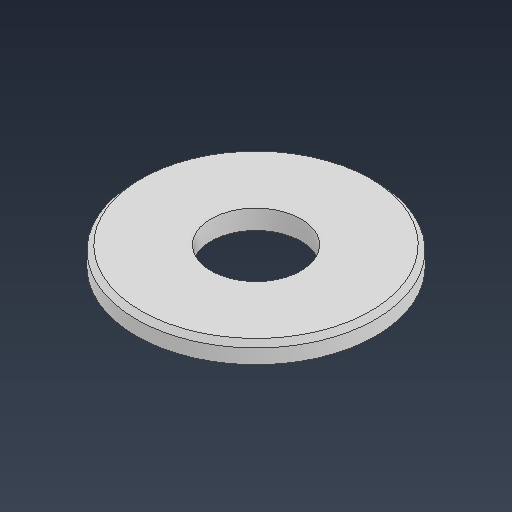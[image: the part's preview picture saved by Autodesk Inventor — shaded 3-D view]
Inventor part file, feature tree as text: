
AUTODESK INVENTOR PART (.ipt)
format: ipt  version: 2021 (Build 250183000, 183)  size: 84,992 bytes
history: native  units: in
note: dims shown in document units (in); Inventor stores cm internally (conversion verified against a paired STEP export)
features: chamfer x1
ambient origin geometry x8: Origin, YZ Plane, XZ Plane, XY Plane, X Axis, Y Axis, Z Axis, Center Point
bodies: Solid1 (feature_tree)
feature tree (1):
  chamfer  "Chamfer1"  [1 undecoded]
note: 1 required parameter value undecoded (feature->parameter linkage not recoverable at this tier; creation-order binding heuristic only, values carry confidence <= 0.55)
